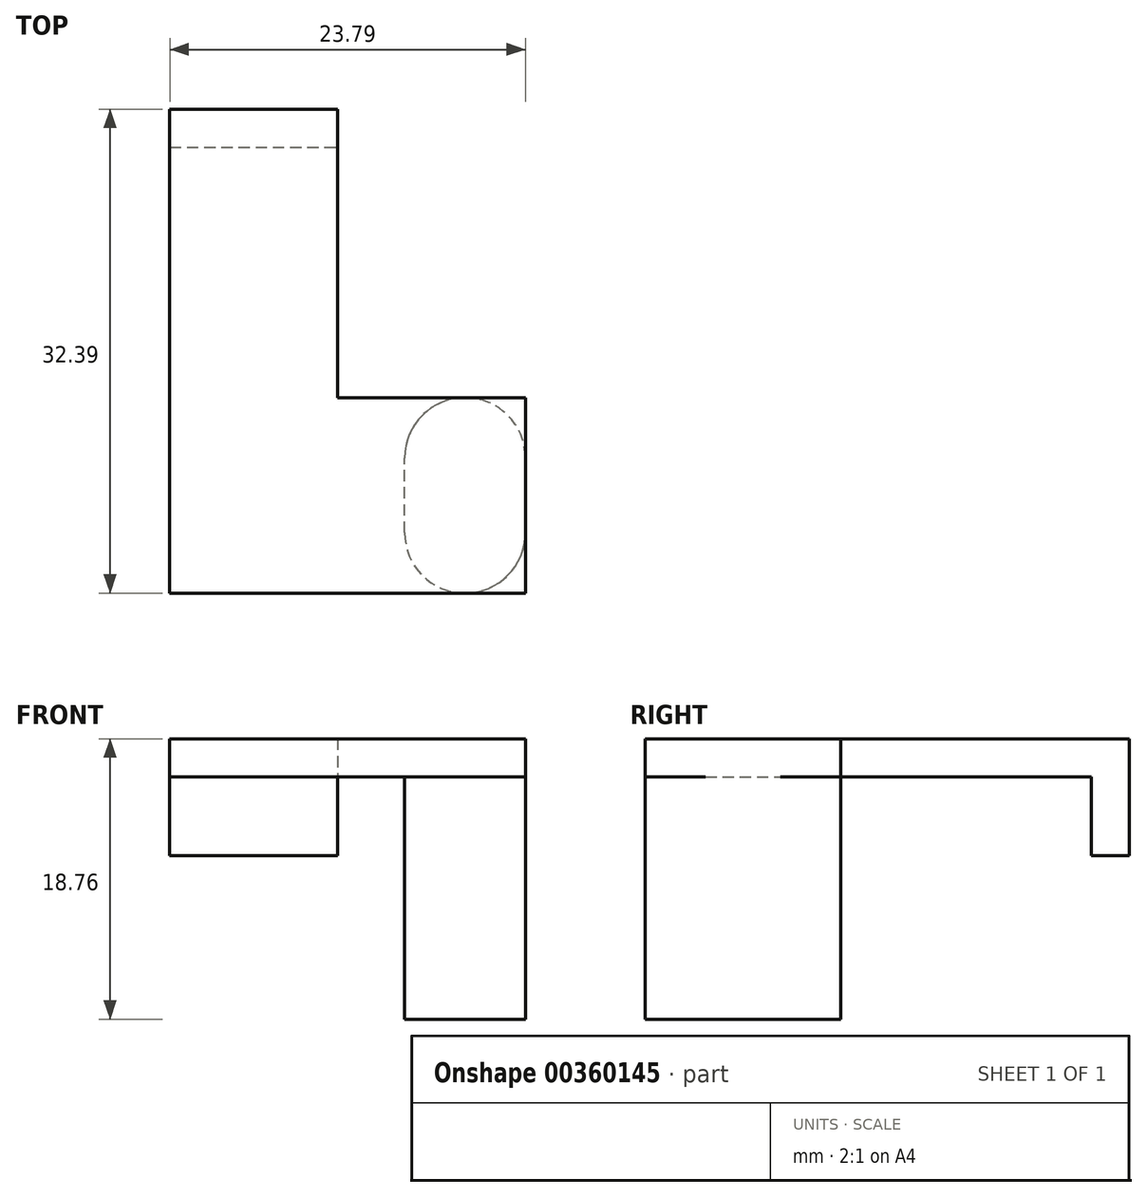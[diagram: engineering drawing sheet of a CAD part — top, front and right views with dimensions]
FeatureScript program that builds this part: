
annotation { "Feature Type Name" : "Feature", "Feature Type Description" : "" }
export const myFeature = defineFeature(function(context is Context, id is Id, definition is map)
    precondition{}
    {
        {
            var Q0;
            Q0=qCreatedBy(makeId("Top.planeOp"),FACE);
            var sketch = newSketch(context, id + "F0", { "sketchPlane" : qUnion([Q0])});
            skLineSegment(sketch, "E0", {"start": v(0, 0) * mm, "end": v(0, 5) * mm});
            skLineSegment(sketch, "E1", {"start": v(8.08, 0) * mm, "end": v(8.08, 5) * mm});
            skArc(sketch, "E2", {"start": v(8.08, 5) * mm, "mid": v(4.04, 9.04) * mm, "end": v(0, 5) * mm});
            skArc(sketch, "E3", {"start": v(0, 0) * mm, "mid": v(4.04, -4.04) * mm, "end": v(8.08, 0) * mm});
            skSolve(sketch);
        }
        {
            var Q0;
            Q0=makeQuery(id+"F0.imprint","IMPRINT",FACE,{"disambiguationData":[TD([[makeQuery(id+"F0.imprint","IMPRINT",EDGE,{"derivedFrom":sQuery(id+"F0.wireOp",EDGE,"E0")}),-1.0]])]});
            extrude(context, id + "F1", {"entities" : qUnion([Q0]), "depth" : 16.22 * mm});
        }
        {
            var Q0;
            Q0=makeQuery(id+"F1.opExtrude","CAP_FACE",FACE,{"disambiguationData":[OSD([sQuery(id+"F0.wireOp",EDGE,"E0"),sQuery(id+"F0.wireOp",EDGE,"E1"),sQuery(id+"F0.wireOp",EDGE,"E2"),sQuery(id+"F0.wireOp",EDGE,"E3")])],"isStart":false});
            var sketch = newSketch(context, id + "F2", { "sketchPlane" : qUnion([Q0])});
            skLineSegment(sketch, "E4.bottom", {"start": v(8.08, -4.04) * mm, "end": v(-4.47, -4.04) * mm});
            skLineSegment(sketch, "E4.top", {"start": v(8.08, 9.04) * mm, "end": v(-4.47, 9.04) * mm});
            skLineSegment(sketch, "E4.left", {"start": v(8.08, -4.04) * mm, "end": v(8.08, 9.04) * mm});
            skLineSegment(sketch, "E4.right", {"start": v(-4.47, -4.04) * mm, "end": v(-4.47, 9.04) * mm, "construction": true});
            skLineSegment(sketch, "E5", {"start": v(-4.47, -4.04) * mm, "end": v(-15.71, -4.04) * mm});
            skLineSegment(sketch, "E6", {"start": v(-15.71, -4.04) * mm, "end": v(-15.71, 28.35) * mm});
            skLineSegment(sketch, "E7", {"start": v(-15.71, 28.35) * mm, "end": v(-4.47, 28.35) * mm});
            skLineSegment(sketch, "E8", {"start": v(-4.47, 28.35) * mm, "end": v(-4.47, 9.04) * mm});
            skLineSegment(sketch, "E9", {"start": v(-15.71, 25.8) * mm, "end": v(-4.47, 25.8) * mm});
            skSolve(sketch);
        }
        {
            var Q0;
            {var subQ0=sQuery(id+"F2.wireOp",EDGE,"E4.left");var subQ1=sQuery(id+"F2.wireOp",EDGE,"E4.bottom");var subQ2=makeQuery(id+"F2.imprint","INTERSECT",VERTEX,{"derivedFrom":[subQ1,subQ0]});Q0=makeQuery(id+"F2.imprint","IMPRINT",FACE,{"disambiguationData":[TD([[makeQuery(id+"F2.imprint","IMPRINT",EDGE,{"disambiguationData":[TD([[subQ2,-1.0]])],"derivedFrom":subQ1}),-1.0]])]});}
            var Q1;
            {var subQ0=sQuery(id+"F2.wireOp",EDGE,"E4.left");var subQ1=sQuery(id+"F2.wireOp",EDGE,"E4.top");var subQ2=makeQuery(id+"F2.imprint","INTERSECT",VERTEX,{"derivedFrom":[subQ1,subQ0]});Q1=makeQuery(id+"F2.imprint","IMPRINT",FACE,{"disambiguationData":[TD([[makeQuery(id+"F2.imprint","IMPRINT",EDGE,{"disambiguationData":[TD([[subQ2,-1.0]])],"derivedFrom":subQ1}),1.0]])]});}
            var Q2;
            {var subQ4=makeQuery(id+"F1.opExtrude","CAP_EDGE",EDGE,{"disambiguationData":[OSD([sQuery(id+"F0.wireOp",EDGE,"E0")])],"isStart":false});Q2=makeQuery(id+"F2.imprint","IMPRINT",FACE,{"disambiguationData":[TD([[makeQuery(id+"F2.imprint","IMPRINT",EDGE,{"derivedFrom":subQ4}),-1.0]])]});}
            var Q3;
            {var subQ0=sQuery(id+"F2.wireOp",EDGE,"E5");Q3=makeQuery(id+"F2.imprint","IMPRINT",FACE,{"disambiguationData":[TD([[makeQuery(id+"F2.imprint","IMPRINT",EDGE,{"derivedFrom":subQ0}),-1.0]])]});}
            var Q4;
            {var subQ0=sQuery(id+"F2.wireOp",EDGE,"E7");Q4=makeQuery(id+"F2.imprint","IMPRINT",FACE,{"disambiguationData":[TD([[makeQuery(id+"F2.imprint","IMPRINT",EDGE,{"derivedFrom":subQ0}),-1.0]])]});}
            extrude(context, id + "F3", {"entities" : qUnion([Q0, Q1, Q2, Q3, Q4]), "operationType" : NewBodyOperationType.ADD, "depth" : 2.54 * mm});
        }
        {
            var Q0;
            {var subQ0=sQuery(id+"F2.wireOp",EDGE,"E7");Q0=makeQuery(id+"F2.imprint","IMPRINT",FACE,{"disambiguationData":[TD([[makeQuery(id+"F2.imprint","IMPRINT",EDGE,{"derivedFrom":subQ0}),-1.0]])]});}
            extrude(context, id + "F4", {"entities" : qUnion([Q0]), "operationType" : NewBodyOperationType.ADD, "oppositeDirection" : true, "depth" : 5.28 * mm});
        }
    });
